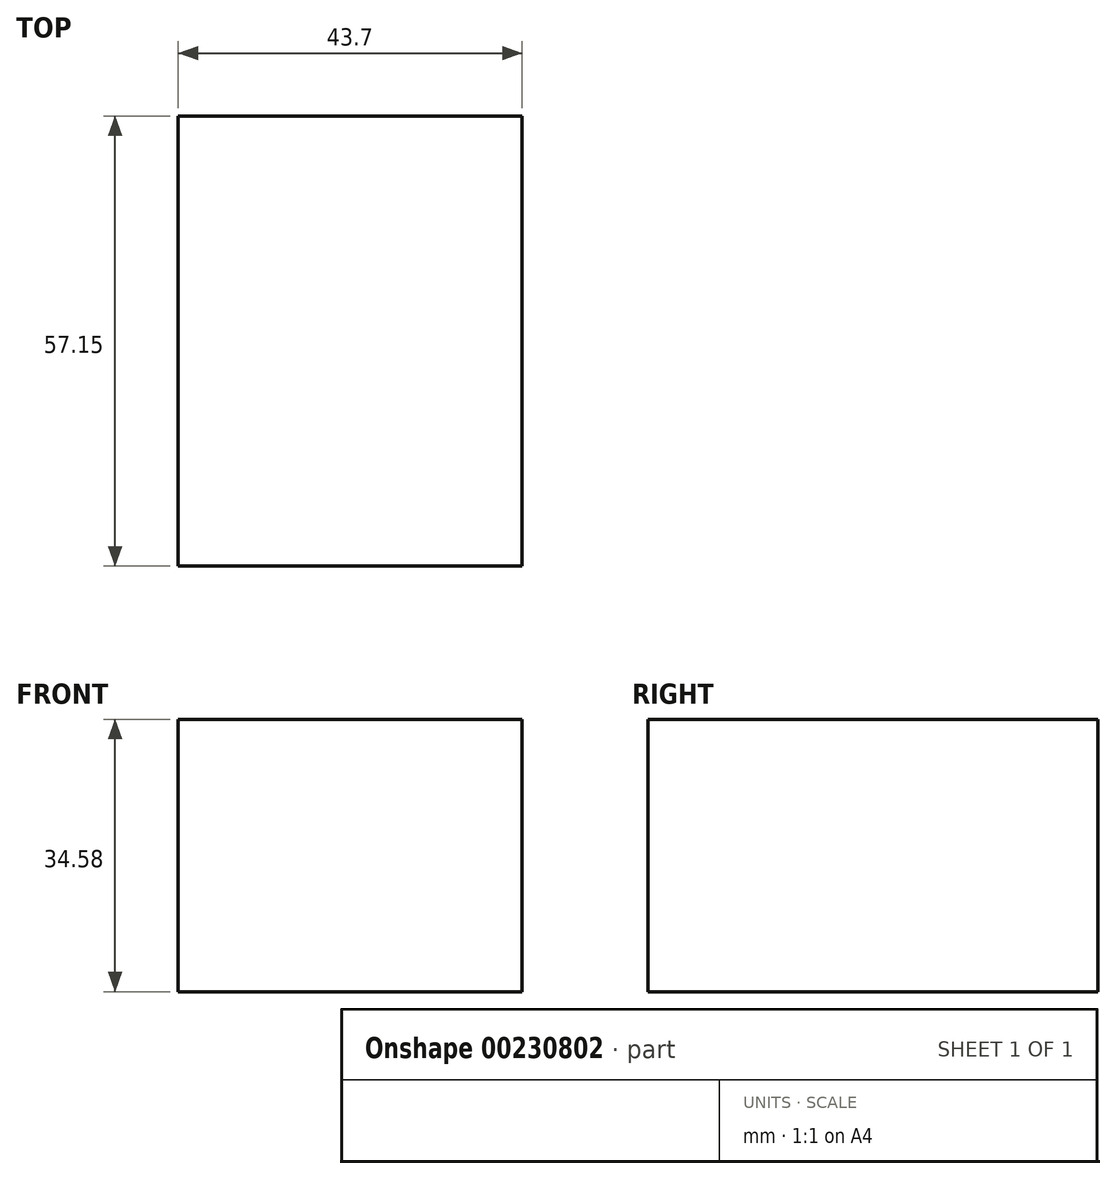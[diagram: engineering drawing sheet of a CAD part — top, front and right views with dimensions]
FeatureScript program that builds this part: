
annotation { "Feature Type Name" : "Feature", "Feature Type Description" : "" }
export const myFeature = defineFeature(function(context is Context, id is Id, definition is map)
    precondition{}
    {
        {
            var Q0;
            Q0=qCreatedBy(makeId("Front.planeOp"),FACE);
            var sketch = newSketch(context, id + "F0", { "sketchPlane" : qUnion([Q0])});
            skLineSegment(sketch, "E0.bottom", {"start": v(-65.11, 54.4) * mm, "end": v(-21.41, 54.4) * mm});
            skLineSegment(sketch, "E0.top", {"start": v(-65.11, 19.82) * mm, "end": v(-21.41, 19.82) * mm});
            skLineSegment(sketch, "E0.left", {"start": v(-65.11, 54.4) * mm, "end": v(-65.11, 19.82) * mm});
            skLineSegment(sketch, "E0.right", {"start": v(-21.41, 54.4) * mm, "end": v(-21.41, 19.82) * mm});
            skSolve(sketch);
        }
        {
            var Q0;
            Q0=makeQuery(id+"F0.imprint","IMPRINT",FACE,{"disambiguationData":[TD([[makeQuery(id+"F0.imprint","IMPRINT",EDGE,{"derivedFrom":sQuery(id+"F0.wireOp",EDGE,"E0.bottom")}),-1.0]])]});
            extrude(context, id + "F1", {"entities" : qUnion([Q0]), "depth" : 57.15 * mm});
        }
    });
